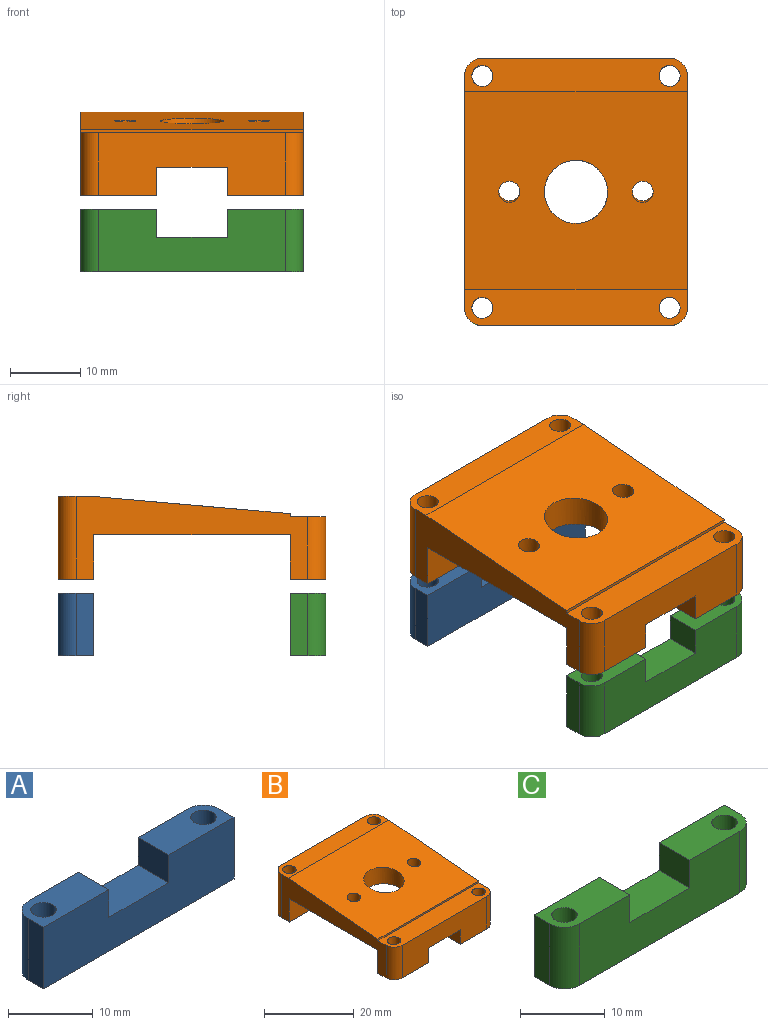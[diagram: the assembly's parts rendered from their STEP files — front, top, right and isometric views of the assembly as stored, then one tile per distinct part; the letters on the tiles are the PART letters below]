
ASSEMBLY  parts=3 mates=2
PART A: 14 faces, bbox 31.8x5.1x8.9 mm
  f0: plane 10.88x5.08mm, normal (0,0,1), area 46.8mm2, adj f1,f2,f3,f4,f6,f13
  f1: plane 31.75x8.89mm, normal (0,-1,0), area 242.3mm2, adj f0,f3,f8,f9,f10,f11,f12,f13
  f2: plane 26.67x8.89mm, normal (0,1,0), area 197.1mm2, adj f0,f4,f5,f9,f10,f11,f12,f13
  f3: plane 8.89x2.54mm, normal (1,0,0), area 22.6mm2, adj f0,f1,f4,f10
  f4: cylinder r=2.54mm len=8.89mm, axis (0,0,-1), area 35.5mm2, adj f0,f2,f3,f10
  f5: cylinder r=2.54mm len=8.89mm, axis (0,0,-1), area 35.5mm2, adj f2,f8,f9,f10
  f6: cylinder r=1.5mm len=8.89mm, axis (0,0,-1), area 83.8mm2, adj f0,f10
  f7: cylinder r=1.5mm len=8.89mm, axis (0,0,-1), area 83.8mm2, adj f9,f10
  f8: plane 8.89x2.54mm, normal (-1,0,0), area 22.6mm2, adj f1,f5,f9,f10
  f9: plane 10.88x5.08mm, normal (0,0,1), area 46.8mm2, adj f1,f2,f5,f7,f8,f11
  f10: plane 31.75x5.08mm, normal (0,0,-1), area 144.4mm2, adj f1,f2,f3,f4,f5,f6,f7,f8
  f11: plane 5.08x4mm, normal (1,0,0), area 20.3mm2, adj f1,f2,f9,f12
  f12: plane 10x5.08mm, normal (0,0,1), area 50.8mm2, adj f1,f2,f11,f13
  f13: plane 5.08x4mm, normal (-1,0,0), area 20.3mm2, adj f0,f1,f2,f12
PART B: 36 faces, bbox 31.8x38.1x11.8 mm
  f0: plane 33.02x11.81mm, normal (1,0,0), area 170.1mm2, adj f1,f5,f15,f16,f17,f18,f19,f21
  f1: plane 31.75x28.31mm, normal (0,-0.09,1), area 824.2mm2, adj f0,f2,f3,f7,f10,f33,f35
  f2: cylinder r=1.5mm len=3.21mm, axis (0,-0.09,1), area 23.9mm2, adj f1,f30
  f3: cylinder r=1.5mm len=3.21mm, axis (0,-0.09,1), area 23.9mm2, adj f1,f32
  f4: plane 26.67x11.81mm, normal (0,1,0), area 275mm2, adj f5,f6,f17,f22,f23,f24,f25,f33
  f5: cylinder r=2.54mm len=11.81mm, axis (0,0,-1), area 47.1mm2, adj f0,f4,f17,f33
  f6: cylinder r=2.54mm len=11.81mm, axis (0,0,-1), area 47.1mm2, adj f4,f7,f22,f33
  f7: plane 33.02x11.81mm, normal (-1,0,0), area 170.1mm2, adj f1,f6,f8,f18,f19,f20,f21,f22
  f8: cylinder r=2.54mm len=8.89mm, axis (0,0,-1), area 35.5mm2, adj f7,f9,f20,f34
  f9: plane 26.67x8.89mm, normal (0,-1,0), area 197.1mm2, adj f8,f15,f16,f20,f26,f27,f28,f34
  f10: cylinder r=4.5mm len=9mm, axis (0,0,-1), area 118.9mm2, adj f1,f18
  f11: cylinder r=1.5mm len=11.81mm, axis (0,0,-1), area 111.3mm2, adj f22,f33
  f12: cylinder r=1.5mm len=11.81mm, axis (0,0,-1), area 111.3mm2, adj f17,f33
  f13: cylinder r=1.5mm len=8.89mm, axis (0,0,-1), area 83.8mm2, adj f20,f34
  f14: cylinder r=1.5mm len=8.89mm, axis (0,0,-1), area 83.8mm2, adj f16,f34
  f15: cylinder r=2.54mm len=8.89mm, axis (0,0,-1), area 35.5mm2, adj f0,f9,f16,f34
  f16: plane 10.88x5.08mm, normal (0,0,-1), area 46.8mm2, adj f0,f9,f14,f15,f19,f27
  f17: plane 10.88x5.08mm, normal (0,0,-1), area 46.8mm2, adj f0,f4,f5,f12,f21,f23
  f18: plane 31.75x27.94mm, normal (0,0,-1), area 784.1mm2, adj f0,f7,f10,f19,f21,f29,f31
  f19: plane 31.75x6.35mm, normal (0,1,0), area 161.6mm2, adj f0,f7,f16,f18,f20,f26,f27,f28
  f20: plane 10.88x5.08mm, normal (0,0,-1), area 46.8mm2, adj f7,f8,f9,f13,f19,f28
  f21: plane 31.75x6.35mm, normal (0,-1,0), area 161.6mm2, adj f0,f7,f17,f18,f22,f23,f24,f25
  f22: plane 10.88x5.08mm, normal (0,0,-1), area 46.8mm2, adj f4,f6,f7,f11,f21,f24
  f23: plane 5.08x4mm, normal (-1,0,0), area 20.3mm2, adj f4,f17,f21,f25
  f24: plane 5.08x4mm, normal (1,0,0), area 20.3mm2, adj f4,f21,f22,f25
  f25: plane 10x5.08mm, normal (0,0,-1), area 50.8mm2, adj f4,f21,f23,f24
  f26: plane 10x5.08mm, normal (0,0,-1), area 50.8mm2, adj f9,f19,f27,f28
  f27: plane 5.08x4mm, normal (-1,0,0), area 20.3mm2, adj f9,f16,f19,f26
  f28: plane 5.08x4mm, normal (1,0,0), area 20.3mm2, adj f9,f19,f20,f26
  f29: cylinder r=2.5mm len=5.15mm, axis (0,-0.09,1), area 26.4mm2, adj f18,f30
  f30: plane 5x4.98mm, normal (0,0.09,-1), area 12.6mm2, adj f2,f29
  f31: cylinder r=2.5mm len=5.15mm, axis (0,-0.09,1), area 26.4mm2, adj f18,f32
  f32: plane 5x4.98mm, normal (0,0.09,-1), area 12.6mm2, adj f3,f31
  f33: plane 31.75x4.71mm, normal (0,0,1), area 132.7mm2, adj f0,f1,f4,f5,f6,f7,f11,f12
  f34: plane 31.75x5.08mm, normal (0,0,1), area 144.4mm2, adj f0,f7,f8,f9,f13,f14,f15,f35
  f35: plane 31.75x0.44mm, normal (0,-1,0), area 14.1mm2, adj f0,f1,f7,f34
PART C: 14 faces, bbox 31.8x5.1x8.9 mm
  f0: plane 10.88x5.08mm, normal (0,0,1), area 46.8mm2, adj f1,f2,f5,f6,f7,f13
  f1: plane 26.67x8.89mm, normal (0,-1,0), area 197.1mm2, adj f0,f4,f5,f9,f10,f11,f12,f13
  f2: plane 31.75x8.89mm, normal (0,1,0), area 242.3mm2, adj f0,f3,f6,f9,f10,f11,f12,f13
  f3: plane 8.89x2.54mm, normal (-1,0,0), area 22.6mm2, adj f2,f4,f9,f10
  f4: cylinder r=2.54mm len=8.89mm, axis (0,0,-1), area 35.5mm2, adj f1,f3,f9,f10
  f5: cylinder r=2.54mm len=8.89mm, axis (0,0,-1), area 35.5mm2, adj f0,f1,f6,f10
  f6: plane 8.89x2.54mm, normal (1,0,0), area 22.6mm2, adj f0,f2,f5,f10
  f7: cylinder r=1.5mm len=8.89mm, axis (0,0,-1), area 83.8mm2, adj f0,f10
  f8: cylinder r=1.5mm len=8.89mm, axis (0,0,-1), area 83.8mm2, adj f9,f10
  f9: plane 10.88x5.08mm, normal (0,0,1), area 46.8mm2, adj f1,f2,f3,f4,f8,f11
  f10: plane 31.75x5.08mm, normal (0,0,-1), area 144.4mm2, adj f1,f2,f3,f4,f5,f6,f7,f8
  f11: plane 5.08x4mm, normal (1,0,0), area 20.3mm2, adj f1,f2,f9,f12
  f12: plane 10x5.08mm, normal (0,0,1), area 50.8mm2, adj f1,f2,f11,f13
  f13: plane 5.08x4mm, normal (-1,0,0), area 20.3mm2, adj f0,f1,f2,f12
PLACE A t=(0,-1.74,-17.24)mm
PLACE B at identity
PLACE C t=(0,-1.74,-17.24)mm
MATE fastened C.f4 <-> B.f8  axis (0,0,1) through (-13.33,-16.51,-8.35)mm
MATE fastened A.f5 <-> B.f6  axis (0,0,1) through (-13.34,16.51,-8.35)mm
